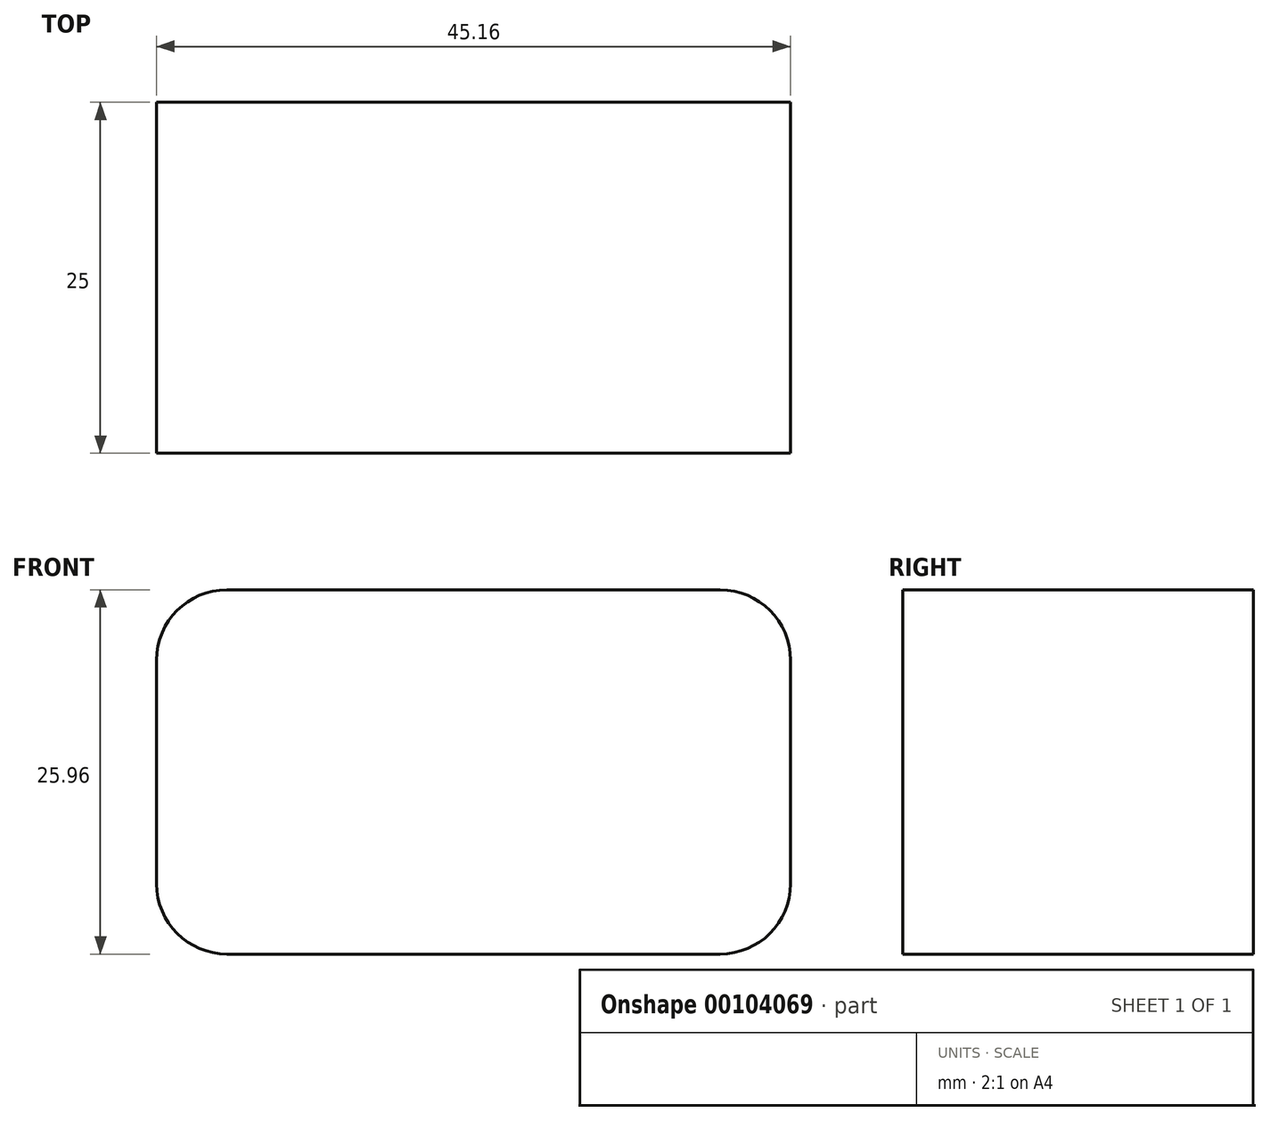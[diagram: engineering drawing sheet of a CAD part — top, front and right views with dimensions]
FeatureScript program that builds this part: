
annotation { "Feature Type Name" : "Feature", "Feature Type Description" : "" }
export const myFeature = defineFeature(function(context is Context, id is Id, definition is map)
    precondition{}
    {
        {
            var Q0;
            Q0=qCreatedBy(makeId("Front.planeOp"),FACE);
            var sketch = newSketch(context, id + "F0", { "sketchPlane" : qUnion([Q0])});
            skLineSegment(sketch, "E0.bottom", {"start": v(-36.12, 11.8) * mm, "end": v(-0.96, 11.8) * mm});
            skLineSegment(sketch, "E0.top", {"start": v(-36.12, -14.16) * mm, "end": v(-0.96, -14.16) * mm});
            skLineSegment(sketch, "E0.left", {"start": v(-41.12, 6.8) * mm, "end": v(-41.12, -9.16) * mm});
            skLineSegment(sketch, "E0.right", {"start": v(4.04, 6.8) * mm, "end": v(4.04, -9.16) * mm});
            skPoint(sketch, "E1.visualSharp", {"position": v(-41.12, 11.8) * mm});
            skArc(sketch, "E1.filletArc", {"start": v(-36.12, 11.8) * mm, "mid": v(-39.66, 10.33) * mm, "end": v(-41.12, 6.8) * mm});
            skPoint(sketch, "E2.visualSharp", {"position": v(4.04, 11.8) * mm});
            skArc(sketch, "E2.filletArc", {"start": v(4.04, 6.8) * mm, "mid": v(2.58, 10.33) * mm, "end": v(-0.96, 11.8) * mm});
            skPoint(sketch, "E3.visualSharp", {"position": v(-41.12, -14.16) * mm});
            skArc(sketch, "E3.filletArc", {"start": v(-41.12, -9.16) * mm, "mid": v(-39.66, -12.7) * mm, "end": v(-36.12, -14.16) * mm});
            skPoint(sketch, "E4.visualSharp", {"position": v(4.04, -14.16) * mm});
            skArc(sketch, "E4.filletArc", {"start": v(-0.96, -14.16) * mm, "mid": v(2.58, -12.7) * mm, "end": v(4.04, -9.16) * mm});
            skSolve(sketch);
        }
        {
            var Q0;
            Q0=makeQuery(id+"F0.imprint","IMPRINT",FACE,{"disambiguationData":[TD([[makeQuery(id+"F0.imprint","IMPRINT",EDGE,{"derivedFrom":sQuery(id+"F0.wireOp",EDGE,"E0.bottom")}),-1.0]])]});
            extrude(context, id + "F1", {"entities" : qUnion([Q0]), "depth" : 25 * mm});
        }
    });
